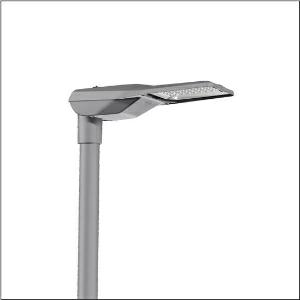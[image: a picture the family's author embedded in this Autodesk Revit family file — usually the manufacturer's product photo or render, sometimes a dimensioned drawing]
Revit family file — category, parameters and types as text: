
# Revit family: streetlight_sl_21_iq_mini___st1_0a_5xe2d31v08gb_747e
name_source: partatom
category: Lighting Fixtures
units: mm (PartAtom-declared; Revit-internal decimal feet)

## family parameters
Cut with Voids When Loaded = No
Host = Face
Light Source = No
Part Type = Normal
Room Calculation Point = No
Round Connector Dimension = Use Diameter
Shared = No

## types (1)
- --- (1 x LED, 5990 lm, 39.8 W, 3000K)
    Apparent Load = 40 VA
    CIE Flux Codes = 37 72 97 100 100
    Color Rendering = 70
    Color Temperature = 3000K
    Default Elevation = 1800 mm
    Description = Streetlight SL 21 iQ mini, mast luminaire, primary light control with lens, of PMMA, primary optical cover: cover, of toughened safety glass, transparent, light distribution: ST1.0a, light emission: direct distribution, primary light characteristic: asymmetric, installation type: post-top, side-entry, LED, High Power LED, rated luminous flux: 5.990lm, luminous efficacy: 151lm/W, light colour: 730, colour temperature: 3000K, control: presetting dimming logarithmic, Street-Remote, Auto-Match, Temp-Guard, Lumen-Switch, Night-Set, Smart-Wire, Light-Fading, Desk-Remote (wireless, voltage-free reading and setting of iQ features in the workshop via application-optimized NFC function/RFID function), optimised constant luminous flux control (CLO 2.0), mains connection: 220..240V, AC, 50/60Hz, start of lifetime: 40W, end of service life: 41W, reduction: 18W, luminaire housing, of diecast aluminium, powder-coated, Siteco® metallic grey (DB 702S), corrosivity category C5 mid according to DIN EN ISO 12944, please order mast flange separately, inclination adjustable: 0°, 5°, 10°, 15°, sealing non-destructively replaceable, multi-level sealing system, length: 628mm, width: 235mm, height: 110mm, mast flange for spigot size: 42mm (side-entry): 5XC10008XM4, 60/48mm (side-entry/post-top): 5XC10108XM2, 76/60mm (side-entry/post-top): 5XC10108XM1, Smart Interface above, protection rating (complete): IP66, insulation class (complete): insulation class II (safety insulation), certification: CE, ENEC, ENEC+, VDE, impact resistance: IK09, permissible operating ambient temperature for outdoor applications: -40..+50°C, standard-compliant lighting for roads and squares, packaging unit: 1 piece

Light Distribution: ST1.0a
    Height = 110 mm
    Lamp = 1 x LED
    Lamp Light Flux = 5990 lm
    Lamp Power = 39.8 W
    Lamp count = 1
    Length = 625 mm
    Luminous efficacy = 151 lm/W
    Manufacturer = Siteco
    ModVariant = No
    Model = 5XE2D31V08GB
    Number of Poles = 1
    OnlyDefault = Yes
    Power Factor = 1
    Product Name = Streetlight SL 21 iQ mini | ST1.0a
    Product group = mast luminaire | pylon top
    ProductGroupID = 6100
    Protection Class = Protection class II
    Protection Degree = IP 66
    RLX_Detail_Level = 1
    RLX_Emergency_Light_Flux = 0 lm
    RLX_Emergency_Type = 0
    RLX_Emergency_Type_DB = No
    RlxData = <blob elided: 93325 chars, md5=bec2af71>
    Socket = socket
    Standby Power = 0 W
    System Light Flux = 5990 lm
    System Power = 40 W
    Type Comments = factory setting: luminous flux: 100 % | dim-lin: 254 | 800 mA
    Type Image = l_1003515.jpg
    URL = http://relux.com
    VarID = @adj_063345
    Voltage = 0 V
    Weight = 0.00 kg
    Width = 234 mm

## geometry (parser evidence)
native form markers: Blend x4, Sweep x12
no freeform markers — native parametric forms only
